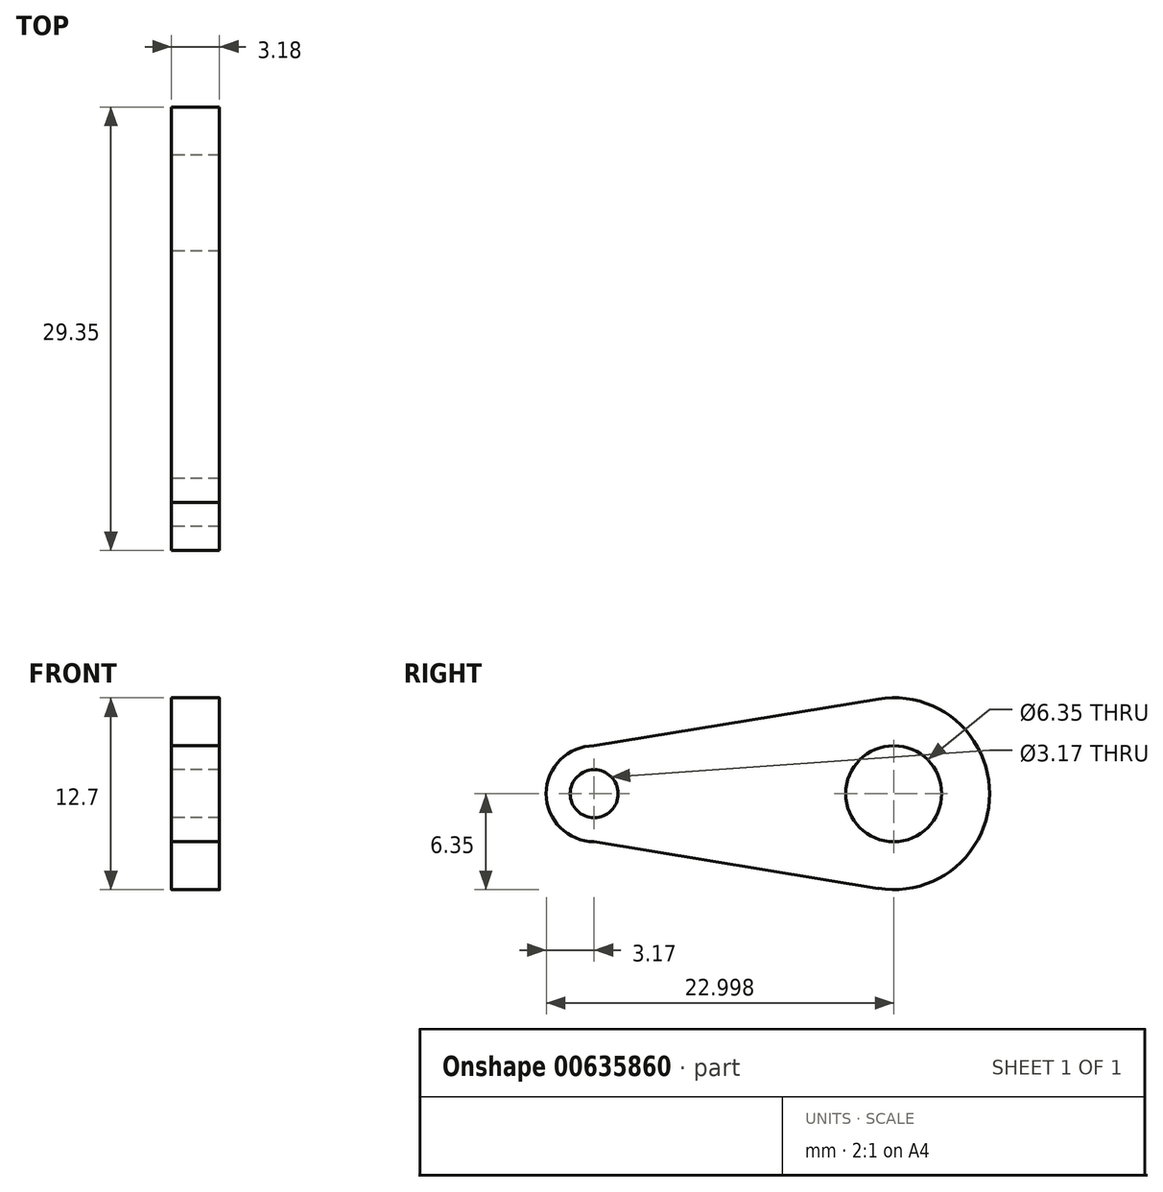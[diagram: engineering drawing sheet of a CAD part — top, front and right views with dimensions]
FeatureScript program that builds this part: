
annotation { "Feature Type Name" : "Feature", "Feature Type Description" : "" }
export const myFeature = defineFeature(function(context is Context, id is Id, definition is map)
    precondition{}
    {
        {
            var Q0;
            Q0=qCreatedBy(makeId("Right.planeOp"),FACE);
            var sketch = newSketch(context, id + "F0", { "sketchPlane" : qUnion([Q0])});
            skCircle(sketch, "E0", {"center": v(0, 0) * mm, "radius": 3.18 * mm});
            skCircle(sketch, "E1", {"center": v(19.83, 0) * mm, "radius": 6.35 * mm});
            skLineSegment(sketch, "E2", {"start": v(0, 3.17) * mm, "end": v(18.8, 6.27) * mm});
            skLineSegment(sketch, "E3", {"start": v(0, -3.17) * mm, "end": v(18.8, -6.27) * mm});
            skCircle(sketch, "E4", {"center": v(0, 0) * mm, "radius": 1.59 * mm});
            skCircle(sketch, "E5", {"center": v(19.83, 0) * mm, "radius": 3.18 * mm});
            skSolve(sketch);
        }
        {
            var Q0;
            {var subQ0=sQuery(id+"F0.wireOp",EDGE,"E2");Q0=makeQuery(id+"F0.imprint","IMPRINT",FACE,{"disambiguationData":[TD([[makeQuery(id+"F0.imprint","IMPRINT",EDGE,{"derivedFrom":subQ0}),-1.0]])]});}
            var Q1;
            Q1=makeQuery(id+"F0.imprint","IMPRINT",FACE,{"disambiguationData":[TD([[makeQuery(id+"F0.imprint","IMPRINT",EDGE,{"derivedFrom":sQuery(id+"F0.wireOp",EDGE,"E4")}),-1.0]])]});
            var Q2;
            Q2=makeQuery(id+"F0.imprint","IMPRINT",FACE,{"disambiguationData":[TD([[makeQuery(id+"F0.imprint","IMPRINT",EDGE,{"derivedFrom":sQuery(id+"F0.wireOp",EDGE,"E5")}),-1.0]])]});
            extrude(context, id + "F1", {"entities" : qUnion([Q0, Q1, Q2]), "depth" : 3.17 * mm, "offsetDistance" : 25.4 * mm});
        }
    });
